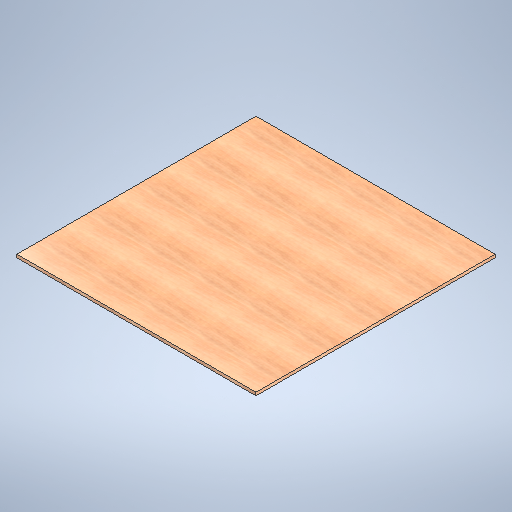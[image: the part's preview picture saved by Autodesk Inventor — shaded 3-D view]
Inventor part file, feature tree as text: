
AUTODESK INVENTOR PART (.ipt)
format: ipt  version: 2025 (Build 290162010, 162A)  size: 332,288 bytes
history: native  units: in
note: dims shown in document units (in); Inventor stores cm internally (conversion verified against a paired STEP export)
features: extrude x1, sketch x1
ambient origin geometry x8: Origin, YZ Plane, XZ Plane, XY Plane, X Axis, Y Axis, Z Axis, Center Point
bodies: Solid1 (feature_tree)
feature tree (2):
  extrude  "Extrusion1"  Depth=48.0in
  sketch  "Sketch1"  dims[d2=48.0in d3=48.0in d4=0.625in d5=0.0in]
